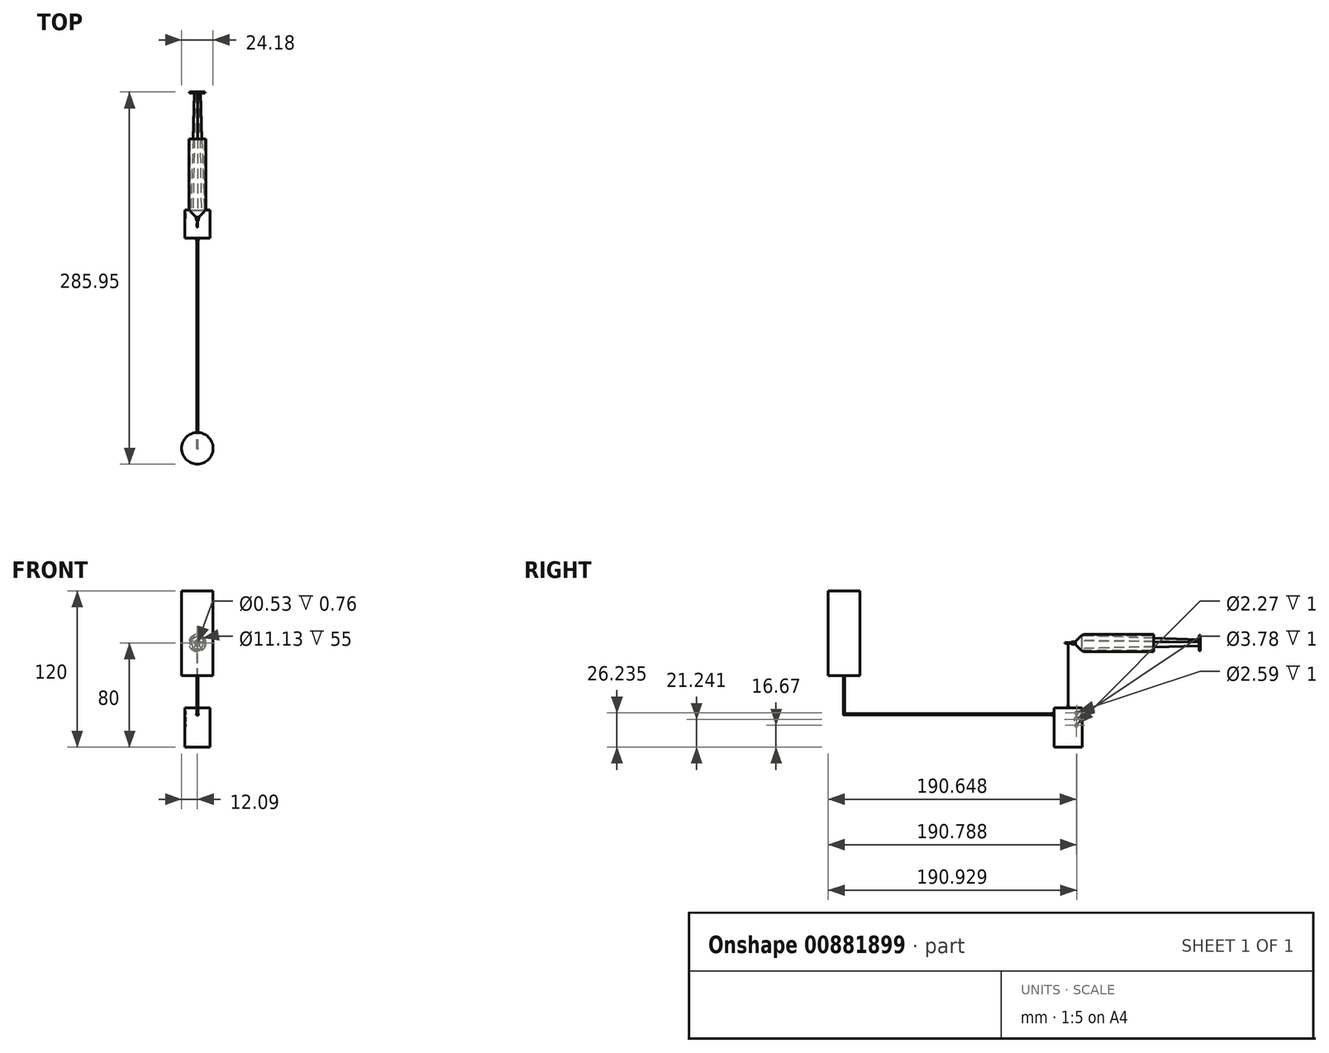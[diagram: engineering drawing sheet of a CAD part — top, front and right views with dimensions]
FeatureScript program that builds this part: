
annotation { "Feature Type Name" : "Feature", "Feature Type Description" : "" }
export const myFeature = defineFeature(function(context is Context, id is Id, definition is map)
    precondition{}
    {
        {
            var Q0;
            Q0=qCreatedBy(makeId("Front.planeOp"),FACE);
            var sketch = newSketch(context, id + "F0", { "sketchPlane" : qUnion([Q0])});
            skCircle(sketch, "E0", {"center": v(0, 0) * mm, "radius": 6.64 * mm});
            skSolve(sketch);
        }
        {
            var Q0;
            Q0 = qSketchRegion(id + "F0", true);
            extrude(context, id + "F1", {"entities" : qUnion([Q0]), "depth" : 60 * mm, "offsetDistance" : 25 * mm});
        }
        {
            var Q0;
            Q0=makeQuery(id+"F1.opExtrude","CAP_FACE",FACE,{"disambiguationData":[OSD([sQuery(id+"F0.wireOp",EDGE,"E0")])],"isStart":true});
            var sketch = newSketch(context, id + "F2", { "sketchPlane" : qUnion([Q0])});
            skCircle(sketch, "E1", {"center": v(0, 0) * mm, "radius": 5.56 * mm});
            skSolve(sketch);
        }
        {
            var Q0;
            Q0 = qSketchRegion(id + "F2", true);
            extrude(context, id + "F3", {"entities" : qUnion([Q0]), "operationType" : NewBodyOperationType.REMOVE, "oppositeDirection" : true, "depth" : 55 * mm, "offsetDistance" : 25 * mm});
        }
        {
            var Q0;
            Q0=makeQuery(id+"F3.boolean.opBoolean","COPY",FACE,{"derivedFrom":makeQuery(id+"F3.opExtrude","CAP_FACE",FACE,{"disambiguationData":[OSD([sQuery(id+"F2.wireOp",EDGE,"E1")])],"isStart":false})});
            var sketch = newSketch(context, id + "F4", { "sketchPlane" : qUnion([Q0])});
            skCircle(sketch, "E2.cCircle", {"center": v(0, 0) * mm, "radius": 4.39 * mm, "construction": true});
            skLineSegment(sketch, "E2.0", {"start": v(-5.22, 1.45) * mm, "end": v(-0.23, 5.42) * mm});
            skLineSegment(sketch, "E2.1", {"start": v(-0.23, 5.42) * mm, "end": v(5.08, 1.9) * mm});
            skLineSegment(sketch, "E2.2", {"start": v(5.08, 1.9) * mm, "end": v(3.37, -4.25) * mm});
            skLineSegment(sketch, "E2.3", {"start": v(3.37, -4.25) * mm, "end": v(-3, -4.52) * mm});
            skLineSegment(sketch, "E2.4", {"start": v(-3, -4.52) * mm, "end": v(-5.22, 1.45) * mm});
            skPoint(sketch, "E2.0.midPoint", {"position": v(-2.73, 3.43) * mm});
            skSolve(sketch);
        }
        {
            var Q0;
            Q0 = qSketchRegion(id + "F4", true);
            extrude(context, id + "F5", {"entities" : qUnion([Q0]), "operationType" : NewBodyOperationType.ADD, "depth" : 90 * mm, "offsetDistance" : 25 * mm, "hasDraft" : true, "draftAngle" : 1.5 * degree, "draftPullDirection" : true});
        }
        {
            var Q0;
            Q0=makeQuery(id+"F5.opExtrude","CAP_FACE",FACE,{"disambiguationData":[OSD([sQuery(id+"F4.wireOp",EDGE,"E2.0"),sQuery(id+"F4.wireOp",EDGE,"E2.1"),sQuery(id+"F4.wireOp",EDGE,"E2.2"),sQuery(id+"F4.wireOp",EDGE,"E2.3"),sQuery(id+"F4.wireOp",EDGE,"E2.4")])],"isStart":false});
            var sketch = newSketch(context, id + "F6", { "sketchPlane" : qUnion([Q0])});
            skCircle(sketch, "E3", {"center": v(0, 0) * mm, "radius": 6 * mm});
            skSolve(sketch);
        }
        {
            var Q0;
            Q0 = qSketchRegion(id + "F6", true);
            extrude(context, id + "F7", {"entities" : qUnion([Q0]), "operationType" : NewBodyOperationType.ADD, "depth" : 1 * mm, "offsetDistance" : 25 * mm});
        }
        {
            var Q0;
            Q0=makeQuery(id+"F1.opExtrude","CAP_EDGE",EDGE,{"disambiguationData":[OSD([sQuery(id+"F0.wireOp",EDGE,"E0")])],"isStart":false});
            chamfer(context, id + "F8", {"entities" : qUnion([Q0]), "width" : 5.5 * mm, "tangentPropagation" : true});
        }
        {
            var Q0;
            {var subQ0=sQuery(id+"F0.wireOp",EDGE,"E0");Q0=makeQuery(id+"F8.opChamfer","BLEND_EDGE",EDGE,{"blendedFrom":[makeQuery(id+"F1.opExtrude","CAP_EDGE",EDGE,{"disambiguationData":[OSD([subQ0])],"isStart":false}),makeQuery(id+"F1.opExtrude","SWEPT_FACE",FACE,{"disambiguationData":[OSD([subQ0])]})],"blendedInto":[makeQuery(id+"F1.opExtrude","SWEPT_FACE",FACE,{"disambiguationData":[OSD([subQ0])]})]});}
            fillet(context, id + "F9", {"entities" : qUnion([Q0]), "radius" : 5 * mm, "tangentPropagation" : true, "allowEdgeOverflow" : false});
        }
        {
            var Q0;
            Q0=makeQuery(id+"F1.opExtrude","CAP_FACE",FACE,{"disambiguationData":[OSD([sQuery(id+"F0.wireOp",EDGE,"E0")])],"isStart":false});
            var sketch = newSketch(context, id + "F10", { "sketchPlane" : qUnion([Q0])});
            skCircle(sketch, "E4", {"center": v(0, 0) * mm, "radius": 1.12 * mm});
            skSolve(sketch);
        }
        {
            var Q0;
            Q0 = qSketchRegion(id + "F10", true);
            extrude(context, id + "F11", {"entities" : qUnion([Q0]), "operationType" : NewBodyOperationType.ADD, "depth" : 3 * mm, "offsetDistance" : 25 * mm, "hasDraft" : true, "draftAngle" : 6 * degree, "draftPullDirection" : true});
        }
        {
            var Q0;
            Q0=makeQuery(id+"F11.opExtrude","CAP_FACE",FACE,{"disambiguationData":[OSD([sQuery(id+"F10.wireOp",EDGE,"E4")])],"isStart":false});
            var sketch = newSketch(context, id + "F12", { "sketchPlane" : qUnion([Q0])});
            skCircle(sketch, "E5", {"center": v(0, 0) * mm, "radius": 0.27 * mm});
            skSolve(sketch);
        }
        {
            var Q0;
            Q0 = qSketchRegion(id + "F12", true);
            extrude(context, id + "F13", {"entities" : qUnion([Q0]), "depth" : 5 * mm, "offsetDistance" : 25 * mm});
        }
        {
            var Q0;
            Q0=makeQuery(id+"F13.opExtrude","CAP_FACE",FACE,{"disambiguationData":[OSD([sQuery(id+"F12.wireOp",EDGE,"E5")])],"isStart":false});
            var sketch = newSketch(context, id + "F14", { "sketchPlane" : qUnion([Q0])});
            skCircle(sketch, "E6", {"center": v(0, 0) * mm, "radius": 0.3 * mm});
            skSolve(sketch);
        }
        {
            var Q0;
            Q0=makeQuery(id+"F14.imprint","IMPRINT",FACE,{"disambiguationData":[TD([[makeQuery(id+"F14.imprint","IMPRINT",EDGE,{"derivedFrom":sQuery(id+"F14.wireOp",EDGE,"E6")}),1.0]])]});
            var Q1;
            Q1=sQuery(id+"F14.wireOp",EDGE,"E6");
            extrude(context, id + "F15", {"entities" : qUnion([Q0]), "surfaceEntities" : qUnion([Q1]), "oppositeDirection" : true, "depth" : 1.46 * mm, "offsetDistance" : 25 * mm, "hasSecondDirection" : true, "secondDirectionOppositeDirection" : true, "secondDirectionDepth" : 0.7 * mm});
        }
        {
            var Q0;
            Q0=makeQuery(id+"F13.opExtrude","CAP_FACE",FACE,{"disambiguationData":[OSD([sQuery(id+"F12.wireOp",EDGE,"E5")])],"isStart":false});
            var sketch = newSketch(context, id + "F16", { "sketchPlane" : qUnion([Q0])});
            skCircle(sketch, "E7", {"center": v(0, 0) * mm, "radius": 0.3 * mm});
            skSolve(sketch);
        }
        {
            var Q0;
            Q0 = qSketchRegion(id + "F16", true);
            var Q1;
            Q1=sQuery(id+"F16.wireOp",EDGE,"E7");
            extrude(context, id + "F17", {"entities" : qUnion([Q0]), "surfaceEntities" : qUnion([Q1]), "oppositeDirection" : true, "depth" : 2.8 * mm, "offsetDistance" : 25 * mm, "hasSecondDirection" : true, "secondDirectionOppositeDirection" : true, "secondDirectionDepth" : 2 * mm});
        }
        {
            var Q0;
            Q0=makeQuery(id+"F13.opExtrude","SWEPT_BODY",BODY,{"disambiguationData":[OSD([sQuery(id+"F12.wireOp",EDGE,"E5")])]});
            var Q1;
            Q1=makeQuery(id+"F15.opExtrude","SWEPT_BODY",BODY,{"disambiguationData":[OSD([sQuery(id+"F12.wireOp",EDGE,"E5"),sQuery(id+"F14.wireOp",EDGE,"E6")])]});
            var Q2;
            Q2=makeQuery(id+"F17.opExtrude","SWEPT_BODY",BODY,{"disambiguationData":[OSD([sQuery(id+"F16.wireOp",EDGE,"E7")])]});
            booleanBodies(context, id + "F18", {"operationType" : BooleanOperationType.INTERSECTION, "tools" : qUnion([Q0, Q1, Q2]), "keepTools" : true});
        }
        {
            var Q0;
            Q0=qCreatedBy(makeId("Top.planeOp"),FACE);
            var sketch = newSketch(context, id + "F19", { "sketchPlane" : qUnion([Q0])});
            skCircle(sketch, "E8", {"center": v(0, -65.6) * mm, "radius": 0.13 * mm});
            skSolve(sketch);
        }
        {
            var Q0;
            Q0 = qSketchRegion(id + "F19", true);
            var Q1;
            Q1=sQuery(id+"F19.wireOp",EDGE,"E8");
            extrude(context, id + "F20", {"entities" : qUnion([Q0]), "surfaceEntities" : qUnion([Q1]), "oppositeDirection" : true, "depth" : 50 * mm, "offsetDistance" : 25 * mm});
        }
        {
            var Q0;
            Q0=makeQuery(id+"F20.opExtrude","CAP_FACE",FACE,{"disambiguationData":[OSD([sQuery(id+"F19.wireOp",EDGE,"E8")])],"isStart":false});
            var sketch = newSketch(context, id + "F21", { "sketchPlane" : qUnion([Q0])});
            skLineSegment(sketch, "E9.bottom", {"start": v(-9.8, 76.34) * mm, "end": v(9.8, 76.34) * mm});
            skLineSegment(sketch, "E9.top", {"start": v(-9.8, 54.88) * mm, "end": v(9.8, 54.88) * mm});
            skLineSegment(sketch, "E9.left", {"start": v(-9.8, 76.34) * mm, "end": v(-9.8, 54.88) * mm});
            skLineSegment(sketch, "E9.right", {"start": v(9.8, 76.34) * mm, "end": v(9.8, 54.88) * mm});
            skPoint(sketch, "E9.middle", {"position": v(0, 65.6) * mm});
            skSolve(sketch);
        }
        {
            var Q0;
            Q0 = qSketchRegion(id + "F21", true);
            extrude(context, id + "F22", {"entities" : qUnion([Q0]), "depth" : 30 * mm, "offsetDistance" : 25 * mm});
        }
        {
            var Q0;
            Q0=makeQuery(id+"F22.opExtrude","CAP_FACE",FACE,{"disambiguationData":[OSD([sQuery(id+"F21.wireOp",EDGE,"E9.bottom"),sQuery(id+"F21.wireOp",EDGE,"E9.top"),sQuery(id+"F21.wireOp",EDGE,"E9.left"),sQuery(id+"F21.wireOp",EDGE,"E9.right")])],"isStart":true});
            var sketch = newSketch(context, id + "F23", { "sketchPlane" : qUnion([Q0])});
            skCircle(sketch, "E10", {"center": v(0, -65.6) * mm, "radius": 0.34 * mm});
            skSolve(sketch);
        }
        {
            var Q0;
            Q0 = qSketchRegion(id + "F23", true);
            extrude(context, id + "F24", {"entities" : qUnion([Q0]), "depth" : 2 * mm, "offsetDistance" : 25 * mm});
        }
        {
            var Q0;
            Q0=makeQuery(id+"F24.opExtrude","CAP_EDGE",EDGE,{"disambiguationData":[OSD([sQuery(id+"F23.wireOp",EDGE,"E10")])],"isStart":false});
            fillet(context, id + "F25", {"entities" : qUnion([Q0]), "radius" : 0.3 * mm, "tangentPropagation" : true, "allowEdgeOverflow" : false});
        }
        {
            var Q0;
            Q0=makeQuery(id+"F22.opExtrude","SWEPT_FACE",FACE,{"disambiguationData":[OSD([sQuery(id+"F21.wireOp",EDGE,"E9.bottom")])]});
            var sketch = newSketch(context, id + "F26", { "sketchPlane" : qUnion([Q0])});
            skCircle(sketch, "E11", {"center": v(0, -54.77) * mm, "radius": 0.86 * mm});
            skSolve(sketch);
        }
        {
            var Q0;
            Q0 = qSketchRegion(id + "F26", true);
            extrude(context, id + "F27", {"entities" : qUnion([Q0]), "depth" : 2 * mm, "offsetDistance" : 25 * mm});
        }
        {
            var Q0;
            Q0=makeQuery(id+"F27.opExtrude","CAP_EDGE",EDGE,{"disambiguationData":[OSD([sQuery(id+"F26.wireOp",EDGE,"E11")])],"isStart":false});
            fillet(context, id + "F28", {"entities" : qUnion([Q0]), "radius" : 0.4 * mm, "tangentPropagation" : true, "allowEdgeOverflow" : false});
        }
        {
            var Q0;
            Q0=makeQuery(id+"F22.opExtrude","SWEPT_FACE",FACE,{"disambiguationData":[OSD([sQuery(id+"F21.wireOp",EDGE,"E9.left")])]});
            var sketch = newSketch(context, id + "F29", { "sketchPlane" : qUnion([Q0])});
            skCircle(sketch, "E12", {"center": v(59.02, -53.77) * mm, "radius": 1.3 * mm});
            skCircle(sketch, "E13", {"center": v(59.16, -58.76) * mm, "radius": 1.89 * mm});
            skCircle(sketch, "E14", {"center": v(59.3, -63.33) * mm, "radius": 1.13 * mm});
            skSolve(sketch);
        }
        {
            var Q0;
            Q0 = qSketchRegion(id + "F29", true);
            extrude(context, id + "F30", {"entities" : qUnion([Q0]), "operationType" : NewBodyOperationType.REMOVE, "oppositeDirection" : true, "depth" : 1 * mm, "offsetDistance" : 25 * mm});
        }
        {
            var Q0;
            Q0=makeQuery(id+"F27.opExtrude","CAP_FACE",FACE,{"disambiguationData":[OSD([sQuery(id+"F26.wireOp",EDGE,"E11")])],"isStart":false});
            var sketch = newSketch(context, id + "F31", { "sketchPlane" : qUnion([Q0])});
            skCircle(sketch, "E15", {"center": v(0, -54.77) * mm, "radius": 0.47 * mm});
            skSolve(sketch);
        }
        {
            var Q0;
            Q0 = qSketchRegion(id + "F31", true);
            extrude(context, id + "F32", {"entities" : qUnion([Q0]), "depth" : 160 * mm, "offsetDistance" : 25 * mm});
        }
        {
            var Q0;
            Q0=qCreatedBy(makeId("Top.planeOp"),FACE);
            var sketch = newSketch(context, id + "F33", { "sketchPlane" : qUnion([Q0])});
            skCircle(sketch, "E16", {"center": v(0, -237.97) * mm, "radius": 0.4 * mm});
            skSolve(sketch);
        }
        {
            var Q0;
            Q0=makeQuery(id+"F33.imprint","IMPRINT",FACE,{"disambiguationData":[TD([[makeQuery(id+"F33.imprint","IMPRINT",EDGE,{"derivedFrom":sQuery(id+"F33.wireOp",EDGE,"E16")}),1.0]])]});
            cPlane(context, id + "F34", {"entities" : qUnion([Q0]), "cplaneType" : CPlaneType.OFFSET, "offset" : 55 * mm, "oppositeDirection" : true, "width" : 150 * mm, "height" : 150 * mm});
        }
        {
            var Q0;
            Q0=qCreatedBy(id+"F34.planeOp",FACE);
            var sketch = newSketch(context, id + "F35", { "sketchPlane" : qUnion([Q0])});
            skCircle(sketch, "E17", {"center": v(0, -237.85) * mm, "radius": 0.44 * mm});
            skSolve(sketch);
        }
        {
            var Q0;
            Q0 = qSketchRegion(id + "F35", true);
            extrude(context, id + "F36", {"entities" : qUnion([Q0]), "operationType" : NewBodyOperationType.ADD, "depth" : 30 * mm, "offsetDistance" : 25 * mm});
        }
        {
            var Q0;
            Q0=makeQuery(id+"F36.boolean.opBoolean","SPLIT",EDGE,{"disambiguationData":[OD(1.0)],"derivedFrom":makeQuery(id+"F36.opExtrude","CAP_EDGE",EDGE,{"disambiguationData":[OSD([sQuery(id+"F35.wireOp",EDGE,"E17")])],"isStart":true})});
            var Q1;
            Q1=makeQuery(id+"F36.boolean.opBoolean","SPLIT",EDGE,{"disambiguationData":[OD(0.0)],"derivedFrom":makeQuery(id+"F36.opExtrude","CAP_EDGE",EDGE,{"disambiguationData":[OSD([sQuery(id+"F35.wireOp",EDGE,"E17")])],"isStart":true})});
            var Q2;
            Q2=makeQuery(id+"F32.opExtrude","CAP_FACE",FACE,{"disambiguationData":[OSD([sQuery(id+"F31.wireOp",EDGE,"E15")])],"isStart":false});
            fillet(context, id + "F37", {"entities" : qUnion([Q0, Q1, Q2]), "radius" : 0.02 * mm, "tangentPropagation" : true, "allowEdgeOverflow" : false});
        }
        {
            var Q0;
            Q0=makeQuery(id+"F36.opExtrude","CAP_FACE",FACE,{"disambiguationData":[OSD([sQuery(id+"F35.wireOp",EDGE,"E17")])],"isStart":false});
            var sketch = newSketch(context, id + "F38", { "sketchPlane" : qUnion([Q0])});
            skCircle(sketch, "E18", {"center": v(0, -237.85) * mm, "radius": 12.1 * mm});
            skSolve(sketch);
        }
        {
            var Q0;
            Q0 = qSketchRegion(id + "F38", true);
            extrude(context, id + "F39", {"entities" : qUnion([Q0]), "operationType" : NewBodyOperationType.ADD, "depth" : 65 * mm, "offsetDistance" : 25 * mm});
        }
    });
